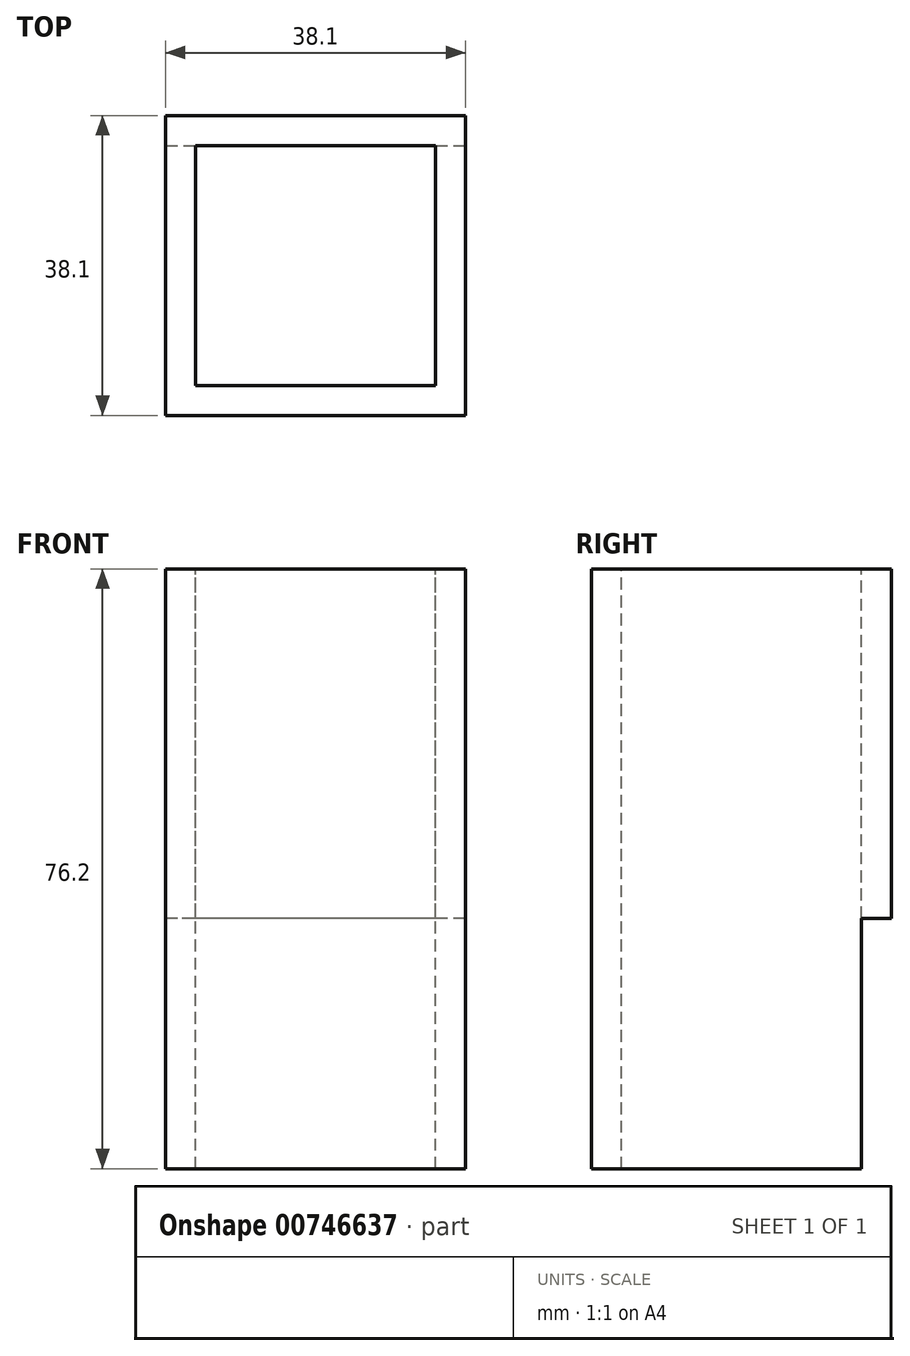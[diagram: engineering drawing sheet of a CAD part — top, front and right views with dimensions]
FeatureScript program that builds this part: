
annotation { "Feature Type Name" : "Feature", "Feature Type Description" : "" }
export const myFeature = defineFeature(function(context is Context, id is Id, definition is map)
    precondition{}
    {
        {
            var Q0;
            Q0=qCreatedBy(makeId("Top.planeOp"),FACE);
            var sketch = newSketch(context, id + "F0", { "sketchPlane" : qUnion([Q0])});
            skLineSegment(sketch, "E0.bottom", {"start": v(0, 0) * mm, "end": v(38.1, 0) * mm});
            skLineSegment(sketch, "E0.top", {"start": v(0, 38.1) * mm, "end": v(38.1, 38.1) * mm});
            skLineSegment(sketch, "E0.left", {"start": v(0, 0) * mm, "end": v(0, 38.1) * mm});
            skLineSegment(sketch, "E0.right", {"start": v(38.1, 0) * mm, "end": v(38.1, 38.1) * mm});
            skSolve(sketch);
        }
        {
            var Q0;
            Q0 = qSketchRegion(id + "F0", true);
            var Q1;
            Q1=makeQuery(id+"F0.imprint","IMPRINT",FACE,{"disambiguationData":[TD([[makeQuery(id+"F0.imprint","IMPRINT",EDGE,{"derivedFrom":sQuery(id+"F0.wireOp",EDGE,"E0.bottom")}),1.0]])]});
            extrude(context, id + "F1", {"entities" : qUnion([Q0, Q1]), "depth" : 76.2 * mm, "offsetDistance" : 25.4 * mm});
        }
        {
            var Q0;
            Q0=makeQuery(id+"F1.opExtrude","CAP_FACE",FACE,{"disambiguationData":[OSD([sQuery(id+"F0.wireOp",EDGE,"E0.bottom"),sQuery(id+"F0.wireOp",EDGE,"E0.top"),sQuery(id+"F0.wireOp",EDGE,"E0.left"),sQuery(id+"F0.wireOp",EDGE,"E0.right")])],"isStart":false});
            var sketch = newSketch(context, id + "F2", { "sketchPlane" : qUnion([Q0])});
            skLineSegment(sketch, "E1.0", {"start": v(34.3, 34.3) * mm, "end": v(3.8, 34.3) * mm});
            skLineSegment(sketch, "E1.1", {"start": v(34.3, 3.8) * mm, "end": v(34.3, 34.3) * mm});
            skLineSegment(sketch, "E1.2", {"start": v(3.8, 3.8) * mm, "end": v(34.3, 3.8) * mm});
            skLineSegment(sketch, "E1.3", {"start": v(3.8, 34.3) * mm, "end": v(3.8, 3.8) * mm});
            skSolve(sketch);
        }
        {
            var Q0;
            Q0=makeQuery(id+"F2.imprint","IMPRINT",FACE,{"disambiguationData":[TD([[makeQuery(id+"F2.imprint","IMPRINT",EDGE,{"derivedFrom":sQuery(id+"F2.wireOp",EDGE,"E1.0")}),1.0]])]});
            extrude(context, id + "F3", {"entities" : qUnion([Q0]), "operationType" : NewBodyOperationType.REMOVE, "oppositeDirection" : true, "depth" : 88.9 * mm, "offsetDistance" : 25.4 * mm});
        }
        {
            var Q0;
            Q0=makeQuery(id+"F1.opExtrude","SWEPT_FACE",FACE,{"disambiguationData":[OSD([sQuery(id+"F0.wireOp",EDGE,"E0.top")])]});
            var sketch = newSketch(context, id + "F4", { "sketchPlane" : qUnion([Q0])});
            skLineSegment(sketch, "E2.bottom", {"start": v(-38.1, 0) * mm, "end": v(0, 0) * mm});
            skLineSegment(sketch, "E2.top", {"start": v(-38.1, 31.79) * mm, "end": v(0, 31.79) * mm});
            skLineSegment(sketch, "E2.left", {"start": v(-38.1, 0) * mm, "end": v(-38.1, 31.79) * mm});
            skLineSegment(sketch, "E2.right", {"start": v(0, 0) * mm, "end": v(0, 31.79) * mm});
            skSolve(sketch);
        }
        {
            var Q0;
            Q0=makeQuery(id+"F4.imprint","IMPRINT",FACE,{"disambiguationData":[TD([[makeQuery(id+"F4.imprint","IMPRINT",EDGE,{"derivedFrom":sQuery(id+"F4.wireOp",EDGE,"E2.bottom")}),-1.0]])]});
            extrude(context, id + "F5", {"entities" : qUnion([Q0]), "operationType" : NewBodyOperationType.REMOVE, "oppositeDirection" : true, "depth" : 3.8 * mm, "offsetDistance" : 25.4 * mm});
        }
    });
